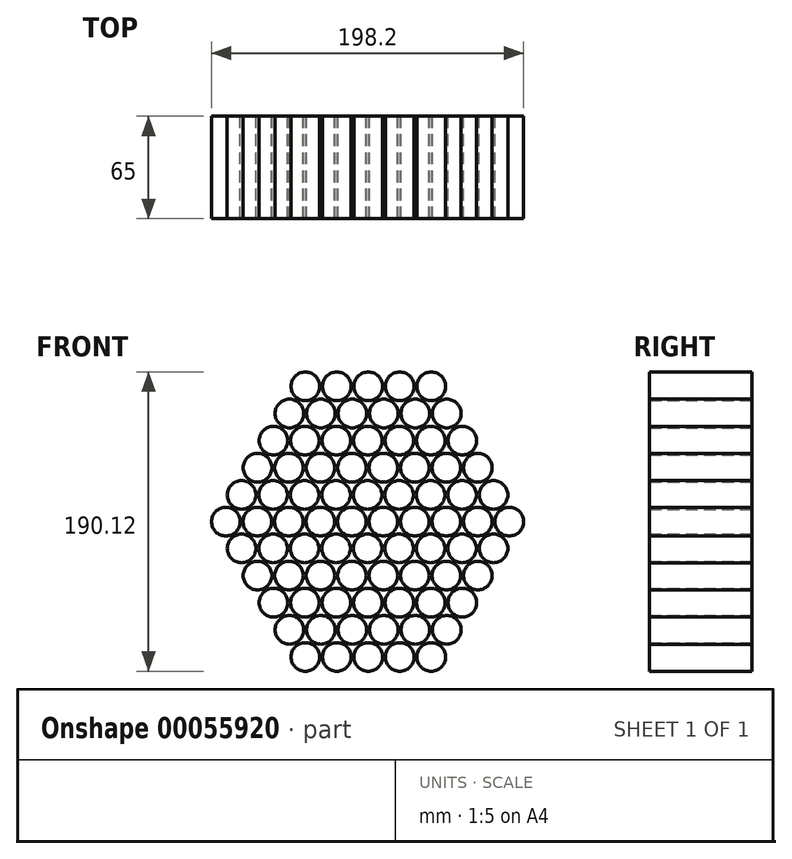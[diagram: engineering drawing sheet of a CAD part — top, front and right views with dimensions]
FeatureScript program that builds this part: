
annotation { "Feature Type Name" : "Feature", "Feature Type Description" : "" }
export const myFeature = defineFeature(function(context is Context, id is Id, definition is map)
    precondition{}
    {
        {
            var Q0;
            Q0=qCreatedBy(makeId("Front.planeOp"),FACE);
            var sketch = newSketch(context, id + "F0", { "sketchPlane" : qUnion([Q0])});
            skCircle(sketch, "E0", {"center": v(0, 0) * mm, "radius": 9.1 * mm});
            skCircle(sketch, "E1.1.0.0", {"center": v(20, 0) * mm, "radius": 9.1 * mm});
            skCircle(sketch, "E1.2.0.0", {"center": v(40, 0) * mm, "radius": 9.1 * mm});
            skCircle(sketch, "E1.3.0.0", {"center": v(60, 0) * mm, "radius": 9.1 * mm});
            skCircle(sketch, "E1.4.0.0", {"center": v(80, 0) * mm, "radius": 9.1 * mm});
            skCircle(sketch, "E1.5.0.0", {"center": v(100, 0) * mm, "radius": 9.1 * mm});
            skCircle(sketch, "E1.6.0.0", {"center": v(120, 0) * mm, "radius": 9.1 * mm});
            skCircle(sketch, "E1.7.0.0", {"center": v(140, 0) * mm, "radius": 9.1 * mm});
            skCircle(sketch, "E1.8.0.0", {"center": v(160, 0) * mm, "radius": 9.1 * mm});
            skCircle(sketch, "E1.9.0.0", {"center": v(180, 0) * mm, "radius": 9.1 * mm});
            skLineSegment(sketch, "E1.direction1", {"start": v(0, 0) * mm, "end": v(20, 0) * mm, "construction": true});
            skCircle(sketch, "E2", {"center": v(10, 17) * mm, "radius": 9.1 * mm});
            skCircle(sketch, "E3.1.0.0", {"center": v(30, 17) * mm, "radius": 9.1 * mm});
            skCircle(sketch, "E3.2.0.0", {"center": v(50, 17) * mm, "radius": 9.1 * mm});
            skCircle(sketch, "E3.3.0.0", {"center": v(70, 17) * mm, "radius": 9.1 * mm});
            skCircle(sketch, "E3.4.0.0", {"center": v(90, 17) * mm, "radius": 9.1 * mm});
            skCircle(sketch, "E3.5.0.0", {"center": v(110, 17) * mm, "radius": 9.1 * mm});
            skCircle(sketch, "E3.6.0.0", {"center": v(130, 17) * mm, "radius": 9.1 * mm});
            skCircle(sketch, "E3.7.0.0", {"center": v(150, 17) * mm, "radius": 9.1 * mm});
            skCircle(sketch, "E3.8.0.0", {"center": v(170, 17) * mm, "radius": 9.1 * mm});
            skLineSegment(sketch, "E3.direction1", {"start": v(10, 17) * mm, "end": v(30, 17) * mm, "construction": true});
            skLineSegment(sketch, "E4", {"start": v(0, 0) * mm, "end": v(10, 17) * mm});
            skLineSegment(sketch, "E5", {"start": v(10, 17) * mm, "end": v(71.53, 121.6) * mm});
            skCircle(sketch, "E6.1.0.0", {"center": v(20.12, 34.24) * mm, "radius": 9.1 * mm});
            skCircle(sketch, "E6.2.0.0", {"center": v(30.24, 51.48) * mm, "radius": 9.1 * mm});
            skCircle(sketch, "E6.3.0.0", {"center": v(40.36, 68.72) * mm, "radius": 9.1 * mm});
            skCircle(sketch, "E6.4.0.0", {"center": v(50.48, 85.96) * mm, "radius": 9.1 * mm});
            skLineSegment(sketch, "E6.direction1", {"start": v(10, 17) * mm, "end": v(20.12, 34.24) * mm, "construction": true});
            skCircle(sketch, "E7.1.0.0", {"center": v(40.1, 34.24) * mm, "radius": 9.1 * mm});
            skCircle(sketch, "E7.2.0.0", {"center": v(60.1, 34.24) * mm, "radius": 9.1 * mm});
            skCircle(sketch, "E7.3.0.0", {"center": v(80.09, 34.24) * mm, "radius": 9.1 * mm});
            skCircle(sketch, "E7.4.0.0", {"center": v(100.08, 34.24) * mm, "radius": 9.1 * mm});
            skCircle(sketch, "E7.5.0.0", {"center": v(120.07, 34.24) * mm, "radius": 9.1 * mm});
            skCircle(sketch, "E7.6.0.0", {"center": v(140.06, 34.24) * mm, "radius": 9.1 * mm});
            skCircle(sketch, "E7.7.0.0", {"center": v(160.05, 34.24) * mm, "radius": 9.1 * mm});
            skLineSegment(sketch, "E7.direction1", {"start": v(20.12, 34.24) * mm, "end": v(40.1, 34.24) * mm, "construction": true});
            skCircle(sketch, "E8.1.0.0", {"center": v(50.23, 51.48) * mm, "radius": 9.1 * mm});
            skCircle(sketch, "E8.2.0.0", {"center": v(70.22, 51.48) * mm, "radius": 9.1 * mm});
            skCircle(sketch, "E8.3.0.0", {"center": v(90.2, 51.48) * mm, "radius": 9.1 * mm});
            skCircle(sketch, "E8.4.0.0", {"center": v(110.2, 51.48) * mm, "radius": 9.1 * mm});
            skCircle(sketch, "E8.5.0.0", {"center": v(130.19, 51.48) * mm, "radius": 9.1 * mm});
            skCircle(sketch, "E8.6.0.0", {"center": v(150.18, 51.48) * mm, "radius": 9.1 * mm});
            skLineSegment(sketch, "E8.direction1", {"start": v(30.24, 51.48) * mm, "end": v(50.23, 51.48) * mm, "construction": true});
            skCircle(sketch, "E9.1.0.0", {"center": v(60.35, 68.72) * mm, "radius": 9.1 * mm});
            skCircle(sketch, "E9.2.0.0", {"center": v(80.34, 68.72) * mm, "radius": 9.1 * mm});
            skCircle(sketch, "E9.3.0.0", {"center": v(100.33, 68.72) * mm, "radius": 9.1 * mm});
            skCircle(sketch, "E9.4.0.0", {"center": v(120.32, 68.72) * mm, "radius": 9.1 * mm});
            skCircle(sketch, "E9.5.0.0", {"center": v(140.3, 68.72) * mm, "radius": 9.1 * mm});
            skLineSegment(sketch, "E9.direction1", {"start": v(40.36, 68.72) * mm, "end": v(60.35, 68.72) * mm, "construction": true});
            skCircle(sketch, "E10.1.0.0", {"center": v(70.47, 85.96) * mm, "radius": 9.1 * mm});
            skCircle(sketch, "E10.2.0.0", {"center": v(90.46, 85.96) * mm, "radius": 9.1 * mm});
            skCircle(sketch, "E10.3.0.0", {"center": v(110.45, 85.96) * mm, "radius": 9.1 * mm});
            skCircle(sketch, "E10.4.0.0", {"center": v(130.44, 85.96) * mm, "radius": 9.1 * mm});
            skLineSegment(sketch, "E10.direction1", {"start": v(50.48, 85.96) * mm, "end": v(70.47, 85.96) * mm, "construction": true});
            skLineSegment(sketch, "E11", {"start": v(0, 0) * mm, "end": v(180, 0) * mm});
            skLineSegment(sketch, "E12.MirrorCS", {"start": v(30.24, -51.48) * mm, "end": v(50.23, -51.48) * mm, "construction": true});
            skLineSegment(sketch, "E13.MirrorCS", {"start": v(50.48, -85.96) * mm, "end": v(70.47, -85.96) * mm, "construction": true});
            skLineSegment(sketch, "E14.MirrorCS", {"start": v(40.36, -68.72) * mm, "end": v(60.35, -68.72) * mm, "construction": true});
            skLineSegment(sketch, "E15.MirrorCS", {"start": v(20.12, -34.24) * mm, "end": v(40.1, -34.24) * mm, "construction": true});
            skCircle(sketch, "E16.MirrorC", {"center": v(160.05, -34.24) * mm, "radius": 9.1 * mm});
            skCircle(sketch, "E17.MirrorC", {"center": v(90.46, -85.96) * mm, "radius": 9.1 * mm});
            skCircle(sketch, "E18.MirrorC", {"center": v(150, -17) * mm, "radius": 9.1 * mm});
            skCircle(sketch, "E19.MirrorC", {"center": v(40.36, -68.72) * mm, "radius": 9.1 * mm});
            skCircle(sketch, "E20.MirrorC", {"center": v(170, -17) * mm, "radius": 9.1 * mm});
            skCircle(sketch, "E21.MirrorC", {"center": v(50.48, -85.96) * mm, "radius": 9.1 * mm});
            skCircle(sketch, "E22.MirrorC", {"center": v(150.18, -51.48) * mm, "radius": 9.1 * mm});
            skCircle(sketch, "E23.MirrorC", {"center": v(130, -17) * mm, "radius": 9.1 * mm});
            skCircle(sketch, "E24.MirrorC", {"center": v(30.24, -51.48) * mm, "radius": 9.1 * mm});
            skCircle(sketch, "E25.MirrorC", {"center": v(130.19, -51.48) * mm, "radius": 9.1 * mm});
            skCircle(sketch, "E26.MirrorC", {"center": v(90, -17) * mm, "radius": 9.1 * mm});
            skCircle(sketch, "E27.MirrorC", {"center": v(70, -17) * mm, "radius": 9.1 * mm});
            skCircle(sketch, "E28.MirrorC", {"center": v(50, -17) * mm, "radius": 9.1 * mm});
            skCircle(sketch, "E29.MirrorC", {"center": v(70.22, -51.48) * mm, "radius": 9.1 * mm});
            skCircle(sketch, "E30.MirrorC", {"center": v(80.09, -34.24) * mm, "radius": 9.1 * mm});
            skCircle(sketch, "E31.MirrorC", {"center": v(120.32, -68.72) * mm, "radius": 9.1 * mm});
            skCircle(sketch, "E32.MirrorC", {"center": v(120.07, -34.24) * mm, "radius": 9.1 * mm});
            skCircle(sketch, "E33.MirrorC", {"center": v(110, -17) * mm, "radius": 9.1 * mm});
            skCircle(sketch, "E34.MirrorC", {"center": v(110.2, -51.48) * mm, "radius": 9.1 * mm});
            skCircle(sketch, "E35.MirrorC", {"center": v(20.12, -34.24) * mm, "radius": 9.1 * mm});
            skCircle(sketch, "E36.MirrorC", {"center": v(50.23, -51.48) * mm, "radius": 9.1 * mm});
            skCircle(sketch, "E37.MirrorC", {"center": v(60.1, -34.24) * mm, "radius": 9.1 * mm});
            skCircle(sketch, "E38.MirrorC", {"center": v(130.44, -85.96) * mm, "radius": 9.1 * mm});
            skCircle(sketch, "E39.MirrorC", {"center": v(100.33, -68.72) * mm, "radius": 9.1 * mm});
            skCircle(sketch, "E40.MirrorC", {"center": v(30, -17) * mm, "radius": 9.1 * mm});
            skCircle(sketch, "E41.MirrorC", {"center": v(10, -17) * mm, "radius": 9.1 * mm});
            skLineSegment(sketch, "E42.MirrorCS", {"start": v(10, -17) * mm, "end": v(30, -17) * mm, "construction": true});
            skLineSegment(sketch, "E43.MirrorCS", {"start": v(10, -17) * mm, "end": v(20.12, -34.24) * mm, "construction": true});
            skCircle(sketch, "E44.MirrorC", {"center": v(140.06, -34.24) * mm, "radius": 9.1 * mm});
            skCircle(sketch, "E45.MirrorC", {"center": v(70.47, -85.96) * mm, "radius": 9.1 * mm});
            skCircle(sketch, "E46.MirrorC", {"center": v(90.2, -51.48) * mm, "radius": 9.1 * mm});
            skCircle(sketch, "E47.MirrorC", {"center": v(140.3, -68.72) * mm, "radius": 9.1 * mm});
            skCircle(sketch, "E48.MirrorC", {"center": v(100.08, -34.24) * mm, "radius": 9.1 * mm});
            skCircle(sketch, "E49.MirrorC", {"center": v(40.1, -34.24) * mm, "radius": 9.1 * mm});
            skCircle(sketch, "E50.MirrorC", {"center": v(80.34, -68.72) * mm, "radius": 9.1 * mm});
            skCircle(sketch, "E51.MirrorC", {"center": v(60.35, -68.72) * mm, "radius": 9.1 * mm});
            skCircle(sketch, "E52.MirrorC", {"center": v(110.45, -85.96) * mm, "radius": 9.1 * mm});
            skSolve(sketch);
        }
        {
            var Q0;
            Q0 = qSketchRegion(id + "F0", true);
            extrude(context, id + "F1", {"entities" : qUnion([Q0]), "depth" : 65 * mm});
        }
    });
